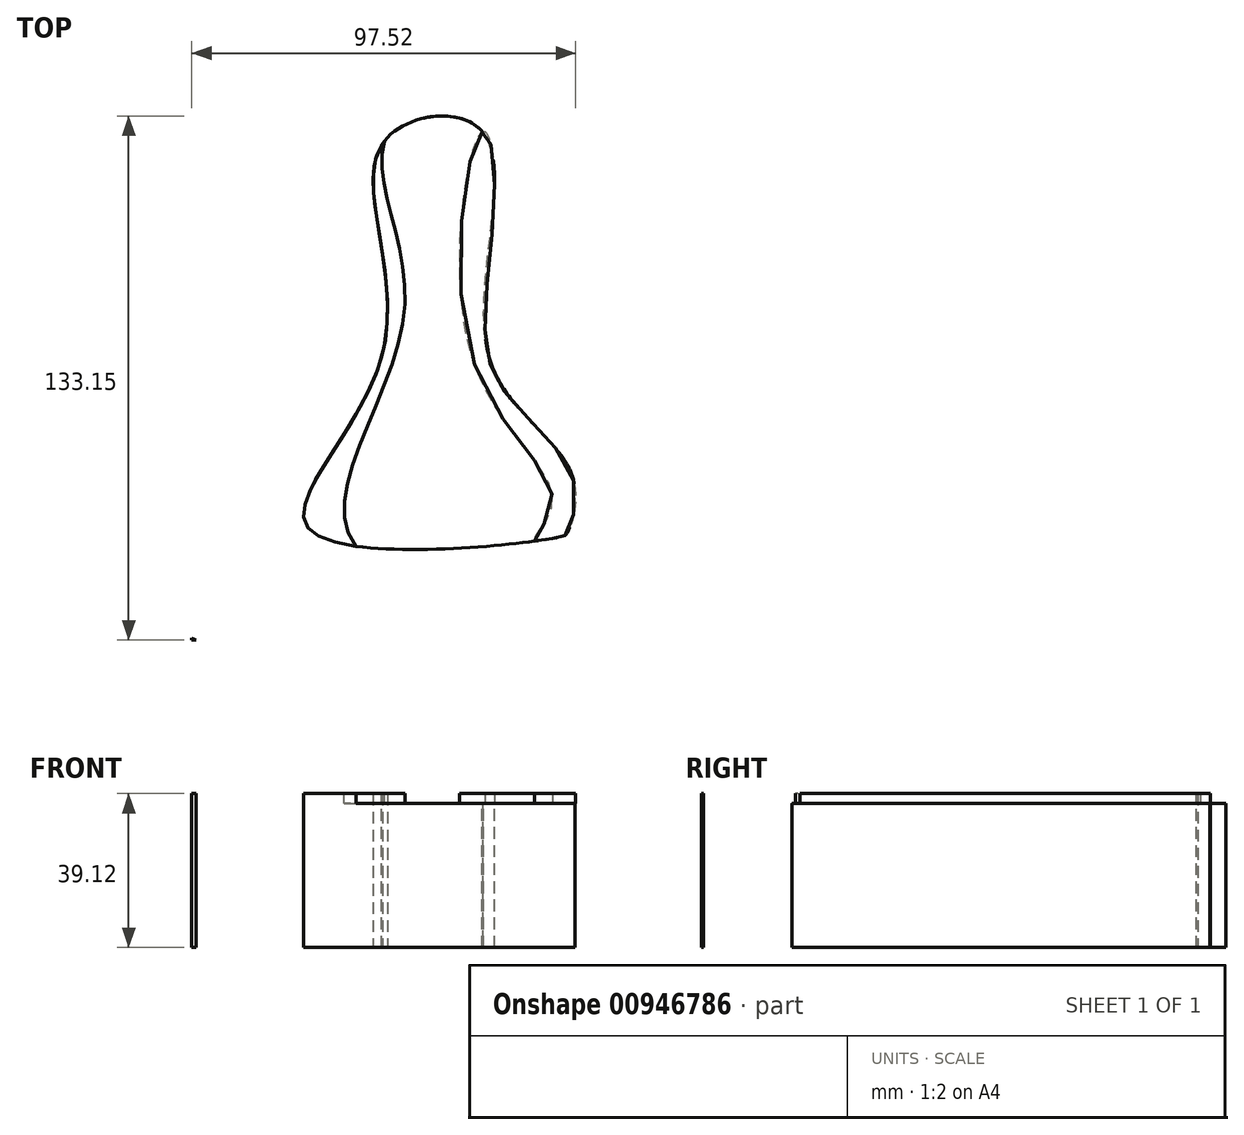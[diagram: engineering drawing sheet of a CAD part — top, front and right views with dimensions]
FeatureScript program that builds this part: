
annotation { "Feature Type Name" : "Feature", "Feature Type Description" : "" }
export const myFeature = defineFeature(function(context is Context, id is Id, definition is map)
    precondition{}
    {
        {
            var Q0;
            Q0=qCreatedBy(makeId("Top.planeOp"),FACE);
            var sketch = newSketch(context, id + "F0", { "sketchPlane" : qUnion([Q0])});
            skLineSegment(sketch, "E0.bottom", {"start": v(-57.64, 68.28) * mm, "end": v(73.6, 68.28) * mm});
            skLineSegment(sketch, "E0.top", {"start": v(-57.64, -72.82) * mm, "end": v(73.6, -72.82) * mm});
            skLineSegment(sketch, "E0.left", {"start": v(-57.64, 68.28) * mm, "end": v(-57.64, -72.82) * mm});
            skLineSegment(sketch, "E0.right", {"start": v(73.6, 68.28) * mm, "end": v(73.6, -72.82) * mm});
            skSolve(sketch);
        }
        {
            var Q0;
            Q0 = qSketchRegion(id + "F0", true);
            extrude(context, id + "F1", {"entities" : qUnion([Q0]), "depth" : 39.12 * mm, "offsetDistance" : 25.4 * mm});
        }
        {
            var Q0;
            Q0=makeQuery(id+"F1.opExtrude","CAP_FACE",FACE,{"disambiguationData":[OSD([sQuery(id+"F0.wireOp",EDGE,"E0.bottom"),sQuery(id+"F0.wireOp",EDGE,"E0.top"),sQuery(id+"F0.wireOp",EDGE,"E0.left"),sQuery(id+"F0.wireOp",EDGE,"E0.right")])],"isStart":false});
            var sketch = newSketch(context, id + "F2", { "sketchPlane" : qUnion([Q0])});
            skFitSpline(sketch, "E1", {"points": [v(-9.16, 53.3) * mm, v(0, 48.77) * mm, v(16.06, 56.46) * mm, v(-9.16, 53.3) * mm]});
            skFitSpline(sketch, "E2", {"points": [v(-9.16, 53.3) * mm, v(-9.16, 0) * mm, v(-27.69, -44.83) * mm, v(35.18, -46.8) * mm, v(38.13, -44.83) * mm, v(38.72, -30.25) * mm, v(17.64, 0) * mm, v(16.06, 56.46) * mm, v(-9.16, 53.3) * mm]});
            skFitSpline(sketch, "E3", {"points": [v(-63.36, -34.2) * mm, v(-60.4, -70.65) * mm, v(14.29, -77.15) * mm, v(77.74, -76.76) * mm, v(76.17, 78.53) * mm, v(-66.7, 68.28) * mm, v(-63.36, -34.2) * mm]});
            skSolve(sketch);
        }
        {
            var Q0;
            Q0 = qSketchRegion(id + "F2", true);
            extrude(context, id + "F3", {"entities" : qUnion([Q0]), "operationType" : NewBodyOperationType.REMOVE, "oppositeDirection" : true, "depth" : 77.72 * mm, "offsetDistance" : 25.4 * mm});
        }
        {
            var Q0;
            {var subQ0=sQuery(id+"F2.wireOp",EDGE,"E2");var subQ1=sQuery(id+"F2.wireOp",EDGE,"E1");var subQ2=makeQuery(id+"F2.imprint","INTERSECT",VERTEX,{"disambiguationData":[OD(0.0)],"derivedFrom":[subQ1,subQ0]});Q0=makeQuery(id+"F3.boolean.opBoolean","SPLIT",FACE,{"disambiguationData":[TD([makeQuery(id+"F3.opExtrude","SWEPT_FACE",FACE,{"disambiguationData":[OSD([subQ1]),TDD([makeQuery(id+"F2.imprint","IMPRINT",EDGE,{"disambiguationData":[TD([[subQ2,1.0]])],"derivedFrom":subQ1})])]})])],"derivedFrom":makeQuery(id+"F1.opExtrude","CAP_FACE",FACE,{"disambiguationData":[OSD([sQuery(id+"F0.wireOp",EDGE,"E0.bottom"),sQuery(id+"F0.wireOp",EDGE,"E0.top"),sQuery(id+"F0.wireOp",EDGE,"E0.left"),sQuery(id+"F0.wireOp",EDGE,"E0.right")])],"isStart":false})});}
            var sketch = newSketch(context, id + "F4", { "sketchPlane" : qUnion([Q0])});
            skFitSpline(sketch, "E4", {"points": [v(-8.68, 53.97) * mm, v(-3.84, 8.77) * mm, v(-15.95, -49) * mm, v(64.93, -41.48) * mm, v(20.2, 64.34) * mm, v(-8.68, 53.97) * mm]});
            skSolve(sketch);
        }
        {
            var Q0;
            Q0 = qSketchRegion(id + "F4", true);
            extrude(context, id + "F5", {"entities" : qUnion([Q0]), "operationType" : NewBodyOperationType.REMOVE, "oppositeDirection" : true, "depth" : 2.54 * mm, "offsetDistance" : 25.4 * mm});
        }
        {
            var Q0;
            Q0=makeQuery(id+"F5.boolean.opBoolean","COPY",FACE,{"derivedFrom":makeQuery(id+"F5.opExtrude","CAP_FACE",FACE,{"disambiguationData":[OSD([sQuery(id+"F4.wireOp",EDGE,"E4")])],"isStart":false})});
            var sketch = newSketch(context, id + "F6", { "sketchPlane" : qUnion([Q0])});
            skFitSpline(sketch, "E5", {"points": [v(29.49, -47.7) * mm, v(34, -38.1) * mm, v(13.74, -1.5) * mm, v(16.18, 56.32) * mm, v(19.27, 43.46) * mm, v(16.96, 3.6) * mm, v(24.25, -12.63) * mm, v(39.53, -33.16) * mm, v(37.2, -46.2) * mm, v(35.27, -46.78) * mm, v(29.49, -47.7) * mm]});
            skSolve(sketch);
        }
        {
            var Q0;
            Q0 = qSketchRegion(id + "F6", true);
            extrude(context, id + "F7", {"entities" : qUnion([Q0]), "operationType" : NewBodyOperationType.ADD, "depth" : 2.54 * mm, "offsetDistance" : 25.4 * mm});
        }
    });
